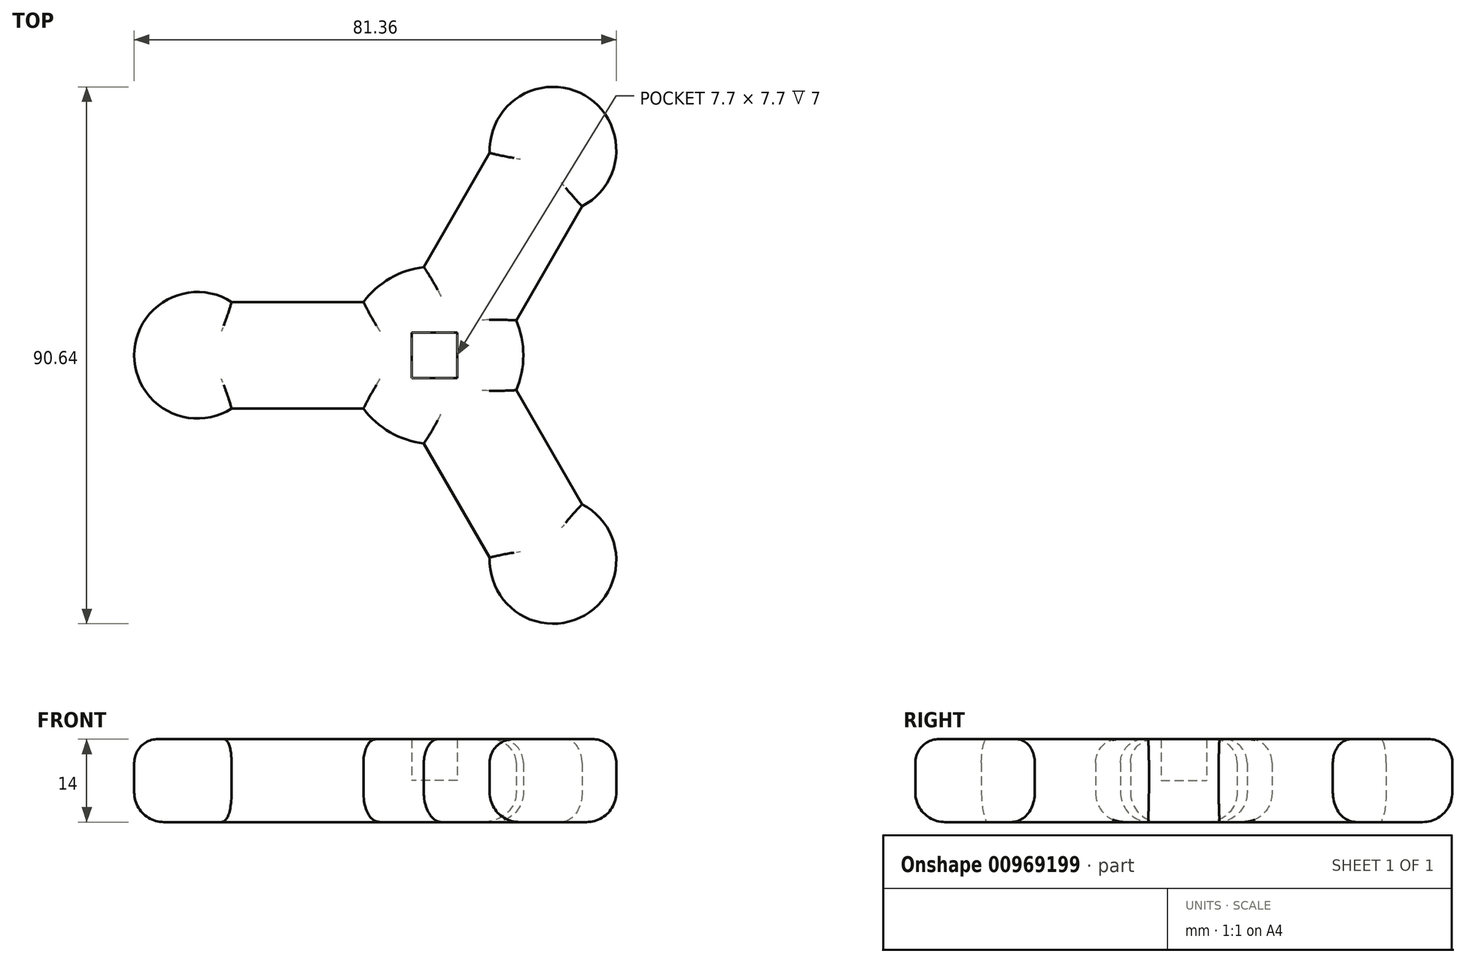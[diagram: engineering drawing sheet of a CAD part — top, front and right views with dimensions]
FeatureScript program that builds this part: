
annotation { "Feature Type Name" : "Feature", "Feature Type Description" : "" }
export const myFeature = defineFeature(function(context is Context, id is Id, definition is map)
    precondition{}
    {
        {
            var Q0;
            Q0=qCreatedBy(makeId("Top.planeOp"),FACE);
            var sketch = newSketch(context, id + "F0", { "sketchPlane" : qUnion([Q0])});
            skLineSegment(sketch, "E0.bottom", {"start": v(3.85, -3.85) * mm, "end": v(-3.85, -3.85) * mm});
            skLineSegment(sketch, "E0.top", {"start": v(3.85, 3.85) * mm, "end": v(-3.85, 3.85) * mm});
            skLineSegment(sketch, "E0.left", {"start": v(3.85, -3.85) * mm, "end": v(3.85, 3.85) * mm});
            skLineSegment(sketch, "E0.right", {"start": v(-3.85, -3.85) * mm, "end": v(-3.85, 3.85) * mm});
            skPoint(sketch, "E0.middle", {"position": v(0, 0) * mm});
            skCircle(sketch, "E1", {"center": v(0, 0) * mm, "radius": 15 * mm});
            skLineSegment(sketch, "E2.bottom", {"start": v(0, 9) * mm, "end": v(-40, 9) * mm});
            skLineSegment(sketch, "E2.top", {"start": v(0, -9) * mm, "end": v(-40, -9) * mm});
            skLineSegment(sketch, "E2.left", {"start": v(0, 9) * mm, "end": v(0, -9) * mm});
            skLineSegment(sketch, "E2.right", {"start": v(-40, 9) * mm, "end": v(-40, -9) * mm});
            skLineSegment(sketch, "E3.1.0", {"start": v(-7.8, -4.5) * mm, "end": v(12.2, -39.14) * mm});
            skLineSegment(sketch, "E3.1.1", {"start": v(-7.8, -4.5) * mm, "end": v(7.8, 4.5) * mm});
            skLineSegment(sketch, "E3.1.2", {"start": v(7.8, 4.5) * mm, "end": v(27.8, -30.14) * mm});
            skLineSegment(sketch, "E3.1.3", {"start": v(12.2, -39.14) * mm, "end": v(27.8, -30.14) * mm});
            skLineSegment(sketch, "E3.2.0", {"start": v(7.8, -4.5) * mm, "end": v(27.8, 30.14) * mm});
            skLineSegment(sketch, "E3.2.1", {"start": v(7.8, -4.5) * mm, "end": v(-7.8, 4.5) * mm});
            skLineSegment(sketch, "E3.2.2", {"start": v(-7.8, 4.5) * mm, "end": v(12.2, 39.14) * mm});
            skLineSegment(sketch, "E3.2.3", {"start": v(27.8, 30.14) * mm, "end": v(12.2, 39.14) * mm});
            skCircle(sketch, "E4", {"center": v(20, 34.64) * mm, "radius": 10.68 * mm});
            skCircle(sketch, "E5.1.0", {"center": v(-40, 0) * mm, "radius": 10.68 * mm});
            skCircle(sketch, "E5.2.0", {"center": v(20, -34.64) * mm, "radius": 10.68 * mm});
            skSolve(sketch);
        }
        {
            var Q0;
            {var subQ0=sQuery(id+"F0.wireOp",EDGE,"E2.right");Q0=makeQuery(id+"F0.imprint","IMPRINT",FACE,{"disambiguationData":[TD([[makeQuery(id+"F0.imprint","IMPRINT",EDGE,{"derivedFrom":subQ0}),-1.0]])]});}
            var Q1;
            {var subQ11=sQuery(id+"F0.wireOp",EDGE,"E0.left");var subQ12=sQuery(id+"F0.wireOp",EDGE,"E0.top");var subQ13=makeQuery(id+"F0.imprint","INTERSECT",VERTEX,{"derivedFrom":[subQ12,subQ11]});Q1=makeQuery(id+"F0.imprint","IMPRINT",FACE,{"disambiguationData":[TD([[makeQuery(id+"F0.imprint","IMPRINT",EDGE,{"disambiguationData":[TD([[subQ13,-1.0]])],"derivedFrom":subQ12}),-1.0]])]});}
            var Q2;
            {var subQ11=sQuery(id+"F0.wireOp",EDGE,"E3.1.1");var subQ12=sQuery(id+"F0.wireOp",EDGE,"E0.right");var subQ13=makeQuery(id+"F0.imprint","INTERSECT",VERTEX,{"derivedFrom":[subQ12,subQ11]});Q2=makeQuery(id+"F0.imprint","IMPRINT",FACE,{"disambiguationData":[TD([[makeQuery(id+"F0.imprint","IMPRINT",EDGE,{"disambiguationData":[TD([[subQ13,-1.0]])],"derivedFrom":subQ12}),1.0]])]});}
            var Q3;
            {var subQ0=sQuery(id+"F0.wireOp",EDGE,"E3.1.0");var subQ1=sQuery(id+"F0.wireOp",EDGE,"E1");var subQ2=makeQuery(id+"F0.imprint","INTERSECT",VERTEX,{"derivedFrom":[subQ1,subQ0]});Q3=makeQuery(id+"F0.imprint","IMPRINT",FACE,{"disambiguationData":[TD([[makeQuery(id+"F0.imprint","IMPRINT",EDGE,{"disambiguationData":[TD([[subQ2,-1.0]])],"derivedFrom":subQ1}),-1.0]])]});}
            var Q4;
            {var subQ0=sQuery(id+"F0.wireOp",EDGE,"E3.2.3");Q4=makeQuery(id+"F0.imprint","IMPRINT",FACE,{"disambiguationData":[TD([[makeQuery(id+"F0.imprint","IMPRINT",EDGE,{"derivedFrom":subQ0}),-1.0]])]});}
            var Q5;
            {var subQ0=sQuery(id+"F0.wireOp",EDGE,"E2.right");Q5=makeQuery(id+"F0.imprint","IMPRINT",FACE,{"disambiguationData":[TD([[makeQuery(id+"F0.imprint","IMPRINT",EDGE,{"derivedFrom":subQ0}),1.0]])]});}
            var Q6;
            {var subQ0=sQuery(id+"F0.wireOp",EDGE,"E2.top");var subQ1=sQuery(id+"F0.wireOp",EDGE,"E1");var subQ2=makeQuery(id+"F0.imprint","INTERSECT",VERTEX,{"derivedFrom":[subQ1,subQ0]});Q6=makeQuery(id+"F0.imprint","IMPRINT",FACE,{"disambiguationData":[TD([[makeQuery(id+"F0.imprint","IMPRINT",EDGE,{"disambiguationData":[TD([[subQ2,-1.0]])],"derivedFrom":subQ1}),1.0]])]});}
            var Q7;
            {var subQ0=sQuery(id+"F0.wireOp",EDGE,"E3.2.3");Q7=makeQuery(id+"F0.imprint","IMPRINT",FACE,{"disambiguationData":[TD([[makeQuery(id+"F0.imprint","IMPRINT",EDGE,{"derivedFrom":subQ0}),1.0]])]});}
            var Q8;
            {var subQ5=sQuery(id+"F0.wireOp",EDGE,"E0.left");var subQ6=sQuery(id+"F0.wireOp",EDGE,"E0.bottom");var subQ7=makeQuery(id+"F0.imprint","INTERSECT",VERTEX,{"derivedFrom":[subQ6,subQ5]});Q8=makeQuery(id+"F0.imprint","IMPRINT",FACE,{"disambiguationData":[TD([[makeQuery(id+"F0.imprint","IMPRINT",EDGE,{"disambiguationData":[TD([[subQ7,-1.0]])],"derivedFrom":subQ6}),1.0]])]});}
            var Q9;
            {var subQ0=sQuery(id+"F0.wireOp",EDGE,"E3.2.0");var subQ1=sQuery(id+"F0.wireOp",EDGE,"E1");var subQ2=makeQuery(id+"F0.imprint","INTERSECT",VERTEX,{"derivedFrom":[subQ1,subQ0]});Q9=makeQuery(id+"F0.imprint","IMPRINT",FACE,{"disambiguationData":[TD([[makeQuery(id+"F0.imprint","IMPRINT",EDGE,{"disambiguationData":[TD([[subQ2,1.0]])],"derivedFrom":subQ1}),1.0]])]});}
            var Q10;
            {var subQ5=sQuery(id+"F0.wireOp",EDGE,"E0.bottom");var subQ7=sQuery(id+"F0.wireOp",EDGE,"E0.right");var subQ8=makeQuery(id+"F0.imprint","INTERSECT",VERTEX,{"derivedFrom":[subQ5,subQ7]});Q10=makeQuery(id+"F0.imprint","IMPRINT",FACE,{"disambiguationData":[TD([[makeQuery(id+"F0.imprint","IMPRINT",EDGE,{"disambiguationData":[TD([[subQ8,1.0]])],"derivedFrom":subQ5}),1.0]])]});}
            var Q11;
            {var subQ0=sQuery(id+"F0.wireOp",EDGE,"E3.1.3");Q11=makeQuery(id+"F0.imprint","IMPRINT",FACE,{"disambiguationData":[TD([[makeQuery(id+"F0.imprint","IMPRINT",EDGE,{"derivedFrom":subQ0}),-1.0]])]});}
            var Q12;
            {var subQ7=sQuery(id+"F0.wireOp",EDGE,"E0.right");var subQ9=sQuery(id+"F0.wireOp",EDGE,"E0.top");var subQ11=makeQuery(id+"F0.imprint","INTERSECT",VERTEX,{"derivedFrom":[subQ9,subQ7]});Q12=makeQuery(id+"F0.imprint","IMPRINT",FACE,{"disambiguationData":[TD([[makeQuery(id+"F0.imprint","IMPRINT",EDGE,{"disambiguationData":[TD([[subQ11,1.0]])],"derivedFrom":subQ9}),-1.0]])]});}
            var Q13;
            {var subQ0=sQuery(id+"F0.wireOp",EDGE,"E3.2.2");var subQ1=sQuery(id+"F0.wireOp",EDGE,"E1");var subQ2=makeQuery(id+"F0.imprint","INTERSECT",VERTEX,{"derivedFrom":[subQ1,subQ0]});Q13=makeQuery(id+"F0.imprint","IMPRINT",FACE,{"disambiguationData":[TD([[makeQuery(id+"F0.imprint","IMPRINT",EDGE,{"disambiguationData":[TD([[subQ2,1.0]])],"derivedFrom":subQ1}),-1.0]])]});}
            var Q14;
            {var subQ0=sQuery(id+"F0.wireOp",EDGE,"E3.1.3");Q14=makeQuery(id+"F0.imprint","IMPRINT",FACE,{"disambiguationData":[TD([[makeQuery(id+"F0.imprint","IMPRINT",EDGE,{"derivedFrom":subQ0}),1.0]])]});}
            var Q15;
            {var subQ0=sQuery(id+"F0.wireOp",EDGE,"E3.2.1");var subQ7=sQuery(id+"F0.wireOp",EDGE,"E0.left");var subQ9=makeQuery(id+"F0.imprint","INTERSECT",VERTEX,{"derivedFrom":[subQ7,subQ0]});Q15=makeQuery(id+"F0.imprint","IMPRINT",FACE,{"disambiguationData":[TD([[makeQuery(id+"F0.imprint","IMPRINT",EDGE,{"disambiguationData":[TD([[subQ9,-1.0]])],"derivedFrom":subQ7}),-1.0]])]});}
            var Q16;
            {var subQ0=sQuery(id+"F0.wireOp",EDGE,"E3.2.2");var subQ1=sQuery(id+"F0.wireOp",EDGE,"E1");var subQ2=makeQuery(id+"F0.imprint","INTERSECT",VERTEX,{"derivedFrom":[subQ1,subQ0]});Q16=makeQuery(id+"F0.imprint","IMPRINT",FACE,{"disambiguationData":[TD([[makeQuery(id+"F0.imprint","IMPRINT",EDGE,{"disambiguationData":[TD([[subQ2,-1.0]])],"derivedFrom":subQ1}),1.0]])]});}
            var Q17;
            {var subQ0=sQuery(id+"F0.wireOp",EDGE,"E2.bottom");var subQ1=sQuery(id+"F0.wireOp",EDGE,"E1");var subQ2=makeQuery(id+"F0.imprint","INTERSECT",VERTEX,{"derivedFrom":[subQ1,subQ0]});Q17=makeQuery(id+"F0.imprint","IMPRINT",FACE,{"disambiguationData":[TD([[makeQuery(id+"F0.imprint","IMPRINT",EDGE,{"disambiguationData":[TD([[subQ2,-1.0]])],"derivedFrom":subQ1}),-1.0]])]});}
            var Q18;
            {var subQ0=sQuery(id+"F0.wireOp",EDGE,"E0.left");var subQ1=sQuery(id+"F0.wireOp",EDGE,"E0.top");var subQ2=makeQuery(id+"F0.imprint","INTERSECT",VERTEX,{"derivedFrom":[subQ1,subQ0]});Q18=makeQuery(id+"F0.imprint","IMPRINT",FACE,{"disambiguationData":[TD([[makeQuery(id+"F0.imprint","IMPRINT",EDGE,{"disambiguationData":[TD([[subQ2,-1.0]])],"derivedFrom":subQ1}),1.0]])]});}
            var Q19;
            {var subQ0=sQuery(id+"F0.wireOp",EDGE,"E0.right");var subQ1=sQuery(id+"F0.wireOp",EDGE,"E0.top");var subQ2=makeQuery(id+"F0.imprint","INTERSECT",VERTEX,{"derivedFrom":[subQ1,subQ0]});Q19=makeQuery(id+"F0.imprint","IMPRINT",FACE,{"disambiguationData":[TD([[makeQuery(id+"F0.imprint","IMPRINT",EDGE,{"disambiguationData":[TD([[subQ2,1.0]])],"derivedFrom":subQ1}),1.0]])]});}
            var Q20;
            {var subQ0=sQuery(id+"F0.wireOp",EDGE,"E0.left");var subQ1=sQuery(id+"F0.wireOp",EDGE,"E0.bottom");var subQ2=makeQuery(id+"F0.imprint","INTERSECT",VERTEX,{"derivedFrom":[subQ1,subQ0]});Q20=makeQuery(id+"F0.imprint","IMPRINT",FACE,{"disambiguationData":[TD([[makeQuery(id+"F0.imprint","IMPRINT",EDGE,{"disambiguationData":[TD([[subQ2,-1.0]])],"derivedFrom":subQ1}),-1.0]])]});}
            var Q21;
            {var subQ0=sQuery(id+"F0.wireOp",EDGE,"E0.right");var subQ1=sQuery(id+"F0.wireOp",EDGE,"E0.bottom");var subQ2=makeQuery(id+"F0.imprint","INTERSECT",VERTEX,{"derivedFrom":[subQ1,subQ0]});Q21=makeQuery(id+"F0.imprint","IMPRINT",FACE,{"disambiguationData":[TD([[makeQuery(id+"F0.imprint","IMPRINT",EDGE,{"disambiguationData":[TD([[subQ2,1.0]])],"derivedFrom":subQ1}),-1.0]])]});}
            var Q22;
            {var subQ0=sQuery(id+"F0.wireOp",EDGE,"E3.1.1");var subQ1=sQuery(id+"F0.wireOp",EDGE,"E0.right");var subQ2=makeQuery(id+"F0.imprint","INTERSECT",VERTEX,{"derivedFrom":[subQ1,subQ0]});Q22=makeQuery(id+"F0.imprint","IMPRINT",FACE,{"disambiguationData":[TD([[makeQuery(id+"F0.imprint","IMPRINT",EDGE,{"disambiguationData":[TD([[subQ2,-1.0]])],"derivedFrom":subQ1}),-1.0]])]});}
            var Q23;
            {var subQ0=sQuery(id+"F0.wireOp",EDGE,"E3.2.1");var subQ1=sQuery(id+"F0.wireOp",EDGE,"E0.left");var subQ2=makeQuery(id+"F0.imprint","INTERSECT",VERTEX,{"derivedFrom":[subQ1,subQ0]});Q23=makeQuery(id+"F0.imprint","IMPRINT",FACE,{"disambiguationData":[TD([[makeQuery(id+"F0.imprint","IMPRINT",EDGE,{"disambiguationData":[TD([[subQ2,-1.0]])],"derivedFrom":subQ1}),1.0]])]});}
            extrude(context, id + "F1", {"entities" : qUnion([Q0, Q1, Q2, Q3, Q4, Q5, Q6, Q7, Q8, Q9, Q10, Q11, Q12, Q13, Q14, Q15, Q16, Q17, Q18, Q19, Q20, Q21, Q22, Q23]), "depth" : 14 * mm, "offsetDistance" : 25 * mm});
        }
        {
            var Q0;
            Q0=makeQuery(id+"F1.opExtrude","CAP_FACE",FACE,{"disambiguationData":[OSD([sQuery(id+"F0.wireOp",EDGE,"E1"),sQuery(id+"F0.wireOp",EDGE,"E2.bottom"),sQuery(id+"F0.wireOp",EDGE,"E2.top"),sQuery(id+"F0.wireOp",EDGE,"E3.1.0"),sQuery(id+"F0.wireOp",EDGE,"E3.1.2"),sQuery(id+"F0.wireOp",EDGE,"E3.2.0"),sQuery(id+"F0.wireOp",EDGE,"E3.2.2"),sQuery(id+"F0.wireOp",EDGE,"E4"),sQuery(id+"F0.wireOp",EDGE,"E5.1.0"),sQuery(id+"F0.wireOp",EDGE,"E5.2.0")])],"isStart":false});
            fillet(context, id + "F2", {"entities" : qUnion([Q0]), "radius" : 4 * mm, "tangentPropagation" : true, "allowEdgeOverflow" : false});
        }
        {
            var Q0;
            {var subQ0=sQuery(id+"F0.wireOp",EDGE,"E3.2.1");var subQ1=sQuery(id+"F0.wireOp",EDGE,"E0.left");var subQ2=makeQuery(id+"F0.imprint","INTERSECT",VERTEX,{"derivedFrom":[subQ1,subQ0]});Q0=makeQuery(id+"F0.imprint","IMPRINT",FACE,{"disambiguationData":[TD([[makeQuery(id+"F0.imprint","IMPRINT",EDGE,{"disambiguationData":[TD([[subQ2,-1.0]])],"derivedFrom":subQ1}),1.0]])]});}
            var Q1;
            {var subQ0=sQuery(id+"F0.wireOp",EDGE,"E0.left");var subQ1=sQuery(id+"F0.wireOp",EDGE,"E0.top");var subQ2=makeQuery(id+"F0.imprint","INTERSECT",VERTEX,{"derivedFrom":[subQ1,subQ0]});Q1=makeQuery(id+"F0.imprint","IMPRINT",FACE,{"disambiguationData":[TD([[makeQuery(id+"F0.imprint","IMPRINT",EDGE,{"disambiguationData":[TD([[subQ2,-1.0]])],"derivedFrom":subQ1}),1.0]])]});}
            var Q2;
            {var subQ0=sQuery(id+"F0.wireOp",EDGE,"E0.right");var subQ1=sQuery(id+"F0.wireOp",EDGE,"E0.top");var subQ2=makeQuery(id+"F0.imprint","INTERSECT",VERTEX,{"derivedFrom":[subQ1,subQ0]});Q2=makeQuery(id+"F0.imprint","IMPRINT",FACE,{"disambiguationData":[TD([[makeQuery(id+"F0.imprint","IMPRINT",EDGE,{"disambiguationData":[TD([[subQ2,1.0]])],"derivedFrom":subQ1}),1.0]])]});}
            var Q3;
            {var subQ0=sQuery(id+"F0.wireOp",EDGE,"E3.1.1");var subQ1=sQuery(id+"F0.wireOp",EDGE,"E0.right");var subQ2=makeQuery(id+"F0.imprint","INTERSECT",VERTEX,{"derivedFrom":[subQ1,subQ0]});Q3=makeQuery(id+"F0.imprint","IMPRINT",FACE,{"disambiguationData":[TD([[makeQuery(id+"F0.imprint","IMPRINT",EDGE,{"disambiguationData":[TD([[subQ2,-1.0]])],"derivedFrom":subQ1}),-1.0]])]});}
            var Q4;
            {var subQ0=sQuery(id+"F0.wireOp",EDGE,"E0.right");var subQ1=sQuery(id+"F0.wireOp",EDGE,"E0.bottom");var subQ2=makeQuery(id+"F0.imprint","INTERSECT",VERTEX,{"derivedFrom":[subQ1,subQ0]});Q4=makeQuery(id+"F0.imprint","IMPRINT",FACE,{"disambiguationData":[TD([[makeQuery(id+"F0.imprint","IMPRINT",EDGE,{"disambiguationData":[TD([[subQ2,1.0]])],"derivedFrom":subQ1}),-1.0]])]});}
            var Q5;
            {var subQ0=sQuery(id+"F0.wireOp",EDGE,"E0.left");var subQ1=sQuery(id+"F0.wireOp",EDGE,"E0.bottom");var subQ2=makeQuery(id+"F0.imprint","INTERSECT",VERTEX,{"derivedFrom":[subQ1,subQ0]});Q5=makeQuery(id+"F0.imprint","IMPRINT",FACE,{"disambiguationData":[TD([[makeQuery(id+"F0.imprint","IMPRINT",EDGE,{"disambiguationData":[TD([[subQ2,-1.0]])],"derivedFrom":subQ1}),-1.0]])]});}
            var Q6;
            Q6=makeQuery(id+"F1.opExtrude","CAP_FACE",FACE,{"disambiguationData":[OSD([sQuery(id+"F0.wireOp",EDGE,"E1"),sQuery(id+"F0.wireOp",EDGE,"E2.bottom"),sQuery(id+"F0.wireOp",EDGE,"E2.top"),sQuery(id+"F0.wireOp",EDGE,"E3.1.0"),sQuery(id+"F0.wireOp",EDGE,"E3.1.2"),sQuery(id+"F0.wireOp",EDGE,"E3.2.0"),sQuery(id+"F0.wireOp",EDGE,"E3.2.2"),sQuery(id+"F0.wireOp",EDGE,"E4"),sQuery(id+"F0.wireOp",EDGE,"E5.1.0"),sQuery(id+"F0.wireOp",EDGE,"E5.2.0")])],"isStart":false});
            extrude(context, id + "F3", {"entities" : qUnion([Q0, Q1, Q2, Q3, Q4, Q5]), "operationType" : NewBodyOperationType.REMOVE, "endBound" : BoundingType.UP_TO_SURFACE, "depth" : 12.6 * mm, "endBoundEntityFace" : qUnion([Q6]), "offsetDistance" : 25 * mm, "hasSecondDirection" : true, "secondDirectionOppositeDirection" : false, "secondDirectionDepth" : 7 * mm});
        }
        {
            var Q0;
            Q0=makeQuery(id+"F1.opExtrude","CAP_EDGE",EDGE,{"disambiguationData":[OSD([sQuery(id+"F0.wireOp",EDGE,"E3.1.0")])],"isStart":true});
            var Q1;
            Q1=makeQuery(id+"F1.opExtrude","CAP_EDGE",EDGE,{"disambiguationData":[OSD([sQuery(id+"F0.wireOp",EDGE,"E3.1.2")])],"isStart":true});
            var Q2;
            Q2=makeQuery(id+"F1.opExtrude","CAP_EDGE",EDGE,{"disambiguationData":[OSD([sQuery(id+"F0.wireOp",EDGE,"E3.2.0")])],"isStart":true});
            var Q3;
            Q3=makeQuery(id+"F1.opExtrude","CAP_EDGE",EDGE,{"disambiguationData":[OSD([sQuery(id+"F0.wireOp",EDGE,"E3.2.2")])],"isStart":true});
            var Q4;
            Q4=makeQuery(id+"F1.opExtrude","CAP_EDGE",EDGE,{"disambiguationData":[OSD([sQuery(id+"F0.wireOp",EDGE,"E2.bottom")])],"isStart":true});
            var Q5;
            Q5=makeQuery(id+"F1.opExtrude","CAP_EDGE",EDGE,{"disambiguationData":[OSD([sQuery(id+"F0.wireOp",EDGE,"E2.top")])],"isStart":true});
            var Q6;
            Q6=makeQuery(id+"F1.opExtrude","CAP_EDGE",EDGE,{"disambiguationData":[OSD([sQuery(id+"F0.wireOp",EDGE,"E5.1.0")])],"isStart":true});
            var Q7;
            Q7=makeQuery(id+"F1.opExtrude","CAP_EDGE",EDGE,{"disambiguationData":[OSD([sQuery(id+"F0.wireOp",EDGE,"E4")])],"isStart":true});
            var Q8;
            Q8=makeQuery(id+"F1.opExtrude","CAP_EDGE",EDGE,{"disambiguationData":[OSD([sQuery(id+"F0.wireOp",EDGE,"E5.2.0")])],"isStart":true});
            var Q9;
            {var subQ0=sQuery(id+"F0.wireOp",EDGE,"E1");Q9=makeQuery(id+"F1.opExtrude","CAP_EDGE",EDGE,{"disambiguationData":[OSD([subQ0]),TDD([makeQuery(id+"F0.imprint","IMPRINT",EDGE,{"disambiguationData":[TD([[makeQuery(id+"F0.imprint","INTERSECT",VERTEX,{"derivedFrom":[subQ0,sQuery(id+"F0.wireOp",EDGE,"E3.2.2")]}),-1.0]])],"derivedFrom":subQ0})])],"isStart":true});}
            var Q10;
            {var subQ0=sQuery(id+"F0.wireOp",EDGE,"E1");Q10=makeQuery(id+"F1.opExtrude","CAP_EDGE",EDGE,{"disambiguationData":[OSD([subQ0]),TDD([makeQuery(id+"F0.imprint","IMPRINT",EDGE,{"disambiguationData":[TD([[makeQuery(id+"F0.imprint","INTERSECT",VERTEX,{"derivedFrom":[subQ0,sQuery(id+"F0.wireOp",EDGE,"E2.top")]}),-1.0]])],"derivedFrom":subQ0})])],"isStart":true});}
            var Q11;
            {var subQ0=sQuery(id+"F0.wireOp",EDGE,"E1");Q11=makeQuery(id+"F1.opExtrude","CAP_EDGE",EDGE,{"disambiguationData":[OSD([subQ0]),TDD([makeQuery(id+"F0.imprint","IMPRINT",EDGE,{"disambiguationData":[TD([[makeQuery(id+"F0.imprint","INTERSECT",VERTEX,{"derivedFrom":[subQ0,sQuery(id+"F0.wireOp",EDGE,"E3.2.0")]}),1.0]])],"derivedFrom":subQ0})])],"isStart":true});}
            fillet(context, id + "F4", {"entities" : qUnion([Q0, Q1, Q2, Q3, Q4, Q5, Q6, Q7, Q8, Q9, Q10, Q11]), "radius" : 5 * mm, "allowEdgeOverflow" : false});
        }
    });
